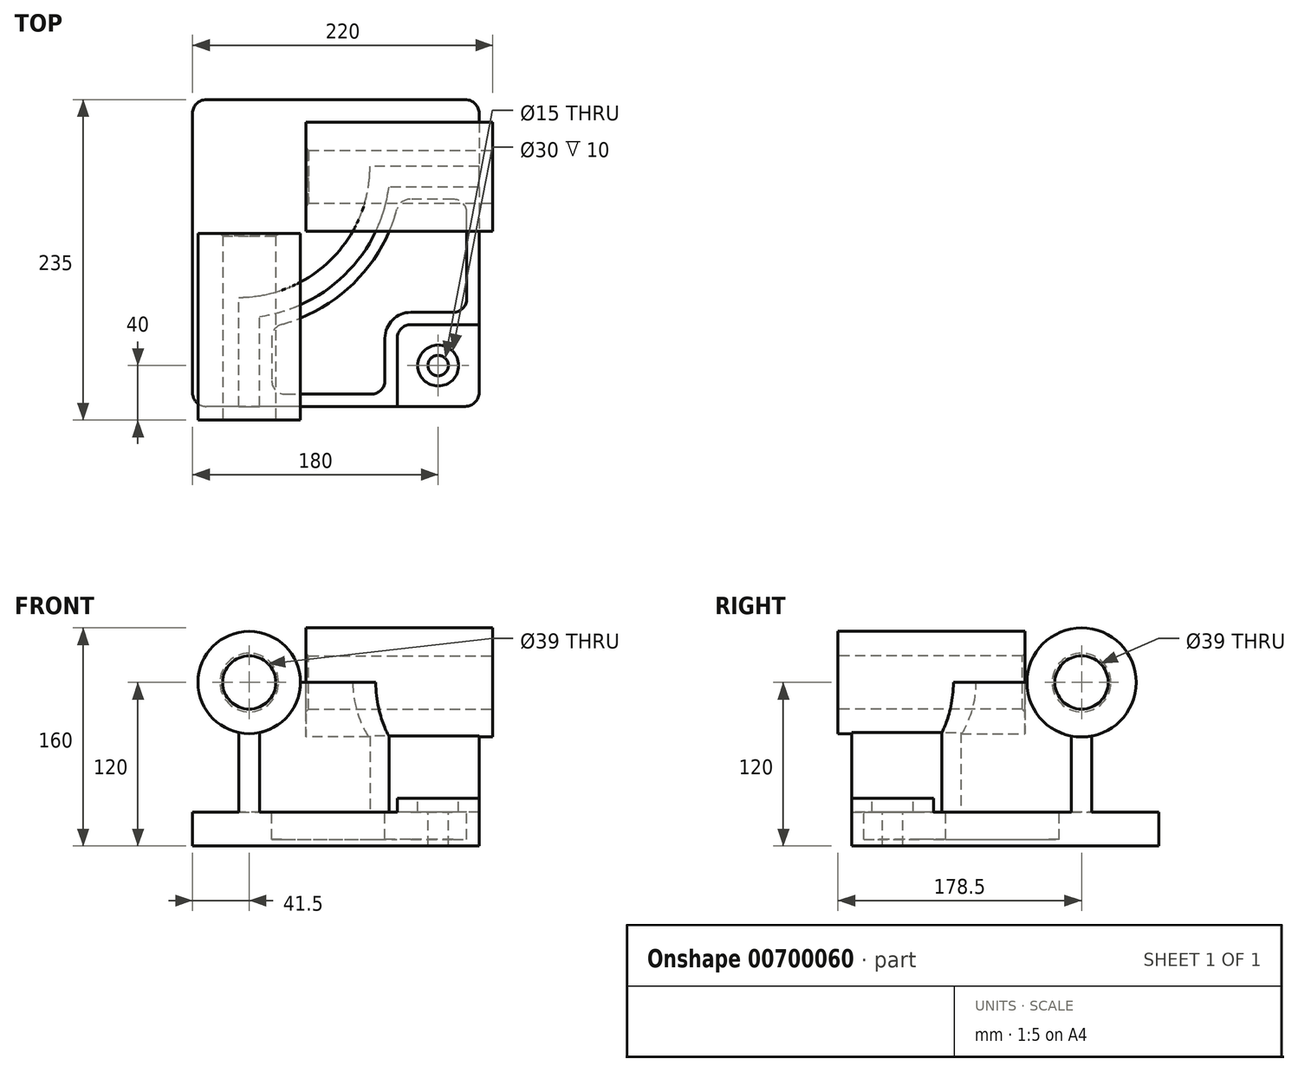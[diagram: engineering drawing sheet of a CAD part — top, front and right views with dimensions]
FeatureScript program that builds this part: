
annotation { "Feature Type Name" : "Feature", "Feature Type Description" : "" }
export const myFeature = defineFeature(function(context is Context, id is Id, definition is map)
    precondition{}
    {
        {
            var Q0;
            Q0=qCreatedBy(makeId("Top.planeOp"),FACE);
            var sketch = newSketch(context, id + "F0", { "sketchPlane" : qUnion([Q0])});
            skLineSegment(sketch, "E0.bottom", {"start": v(105, 112.5) * mm, "end": v(-105, 112.5) * mm});
            skLineSegment(sketch, "E0.top", {"start": v(105, -112.5) * mm, "end": v(-105, -112.5) * mm});
            skLineSegment(sketch, "E0.left", {"start": v(105, 112.5) * mm, "end": v(105, -112.5) * mm});
            skLineSegment(sketch, "E0.right", {"start": v(-105, 112.5) * mm, "end": v(-105, -112.5) * mm});
            skPoint(sketch, "E0.middle", {"position": v(0, 0) * mm});
            skSolve(sketch);
        }
        {
            var Q0;
            Q0=makeQuery(id+"F0.imprint","IMPRINT",FACE,{"disambiguationData":[TD([[makeQuery(id+"F0.imprint","IMPRINT",EDGE,{"derivedFrom":sQuery(id+"F0.wireOp",EDGE,"E0.bottom")}),1.0]])]});
            extrude(context, id + "F1", {"entities" : qUnion([Q0]), "depth" : 25 * mm, "offsetDistance" : 25 * mm});
        }
        {
            var Q0;
            Q0=makeQuery(id+"F1.opExtrude","CAP_FACE",FACE,{"disambiguationData":[OSD([sQuery(id+"F0.wireOp",EDGE,"E0.bottom"),sQuery(id+"F0.wireOp",EDGE,"E0.top"),sQuery(id+"F0.wireOp",EDGE,"E0.left"),sQuery(id+"F0.wireOp",EDGE,"E0.right")])],"isStart":false});
            var sketch = newSketch(context, id + "F2", { "sketchPlane" : qUnion([Q0])});
            skLineSegment(sketch, "E1", {"start": v(-71, -112.5) * mm, "end": v(-71, -32.5) * mm});
            skLineSegment(sketch, "E2", {"start": v(105, 63.5) * mm, "end": v(25, 63.5) * mm});
            skArc(sketch, "E3", {"start": v(-71, -32.5) * mm, "mid": v(-3.12, -4.38) * mm, "end": v(25, 63.5) * mm});
            skLineSegment(sketch, "E4", {"start": v(-71, 63.5) * mm, "end": v(25, 63.5) * mm, "construction": true});
            skLineSegment(sketch, "E5", {"start": v(-71, 63.5) * mm, "end": v(-71, -32.5) * mm, "construction": true});
            skLineSegment(sketch, "E6.0", {"start": v(-56, -112.5) * mm, "end": v(-56, -46.48) * mm});
            skArc(sketch, "E6.1", {"start": v(-56, -46.48) * mm, "mid": v(7.49, -14.99) * mm, "end": v(38.98, 48.5) * mm});
            skLineSegment(sketch, "E6.2", {"start": v(105, 48.5) * mm, "end": v(38.98, 48.5) * mm});
            skLineSegment(sketch, "E7.0", {"start": v(105, 112.5) * mm, "end": v(105, -112.5) * mm});
            skLineSegment(sketch, "E8.0", {"start": v(105, -112.5) * mm, "end": v(-105, -112.5) * mm});
            skSolve(sketch);
        }
        {
            var Q0;
            {var subQ2=sQuery(id+"F2.wireOp",EDGE,"E1");Q0=makeQuery(id+"F2.imprint","IMPRINT",FACE,{"disambiguationData":[TD([[makeQuery(id+"F2.imprint","IMPRINT",EDGE,{"derivedFrom":subQ2}),-1.0]])]});}
            extrude(context, id + "F3", {"entities" : qUnion([Q0]), "operationType" : NewBodyOperationType.ADD, "depth" : 95 * mm, "offsetDistance" : 25 * mm});
        }
        {
            var Q0;
            Q0=makeQuery(id+"F3.boolean.opBoolean","MERGE",FACE,{"derivedFrom":[makeQuery(id+"F1.opExtrude","SWEPT_FACE",FACE,{"disambiguationData":[OSD([sQuery(id+"F0.wireOp",EDGE,"E0.top")])]}),makeQuery(id+"F3.opExtrude","SWEPT_FACE",FACE,{"disambiguationData":[OSD([sQuery(id+"F2.wireOp",EDGE,"E8.0")])]})]});
            var sketch = newSketch(context, id + "F4", { "sketchPlane" : qUnion([Q0])});
            skCircle(sketch, "E9", {"center": v(-63.5, 120) * mm, "radius": 37.5 * mm});
            skSolve(sketch);
        }
        {
            var Q0;
            Q0 = qSketchRegion(id + "F4", true);
            extrude(context, id + "F5", {"entities" : qUnion([Q0]), "operationType" : NewBodyOperationType.ADD, "depth" : 10 * mm, "offsetDistance" : 25 * mm, "hasSecondDirection" : true, "secondDirectionOppositeDirection" : true, "secondDirectionDepth" : (137 - 10) * mm});
        }
        {
            var Q0;
            Q0=makeQuery(id+"F3.boolean.opBoolean","MERGE",FACE,{"derivedFrom":[makeQuery(id+"F1.opExtrude","SWEPT_FACE",FACE,{"disambiguationData":[OSD([sQuery(id+"F0.wireOp",EDGE,"E0.left")])]}),makeQuery(id+"F3.opExtrude","SWEPT_FACE",FACE,{"disambiguationData":[OSD([sQuery(id+"F2.wireOp",EDGE,"E7.0")])]})]});
            var sketch = newSketch(context, id + "F6", { "sketchPlane" : qUnion([Q0])});
            skCircle(sketch, "E10", {"center": v(56, 120) * mm, "radius": 40 * mm});
            skSolve(sketch);
        }
        {
            var Q0;
            Q0 = qSketchRegion(id + "F6", true);
            extrude(context, id + "F7", {"entities" : qUnion([Q0]), "operationType" : NewBodyOperationType.ADD, "depth" : 10 * mm, "offsetDistance" : 25 * mm, "hasSecondDirection" : true, "secondDirectionOppositeDirection" : true, "secondDirectionDepth" : (137 - 10) * mm});
        }
        {
            var Q0;
            {var subQ0=sQuery(id+"F0.wireOp",EDGE,"E0.left");var subQ1=sQuery(id+"F0.wireOp",EDGE,"E0.top");Q0=makeQuery(id+"F3.boolean.opBoolean","SPLIT",FACE,{"disambiguationData":[TD([makeQuery(id+"F3.opExtrude","SWEPT_FACE",FACE,{"disambiguationData":[OSD([sQuery(id+"F2.wireOp",EDGE,"E6.0")])]})])],"derivedFrom":makeQuery(id+"F1.opExtrude","CAP_FACE",FACE,{"disambiguationData":[OSD([sQuery(id+"F0.wireOp",EDGE,"E0.bottom"),subQ1,subQ0,sQuery(id+"F0.wireOp",EDGE,"E0.right")])],"isStart":false})});}
            var sketch = newSketch(context, id + "F8", { "sketchPlane" : qUnion([Q0])});
            skLineSegment(sketch, "E11.bottom", {"start": v(105, -112.5) * mm, "end": v(45, -112.5) * mm});
            skLineSegment(sketch, "E11.top", {"start": v(105, -52.5) * mm, "end": v(45, -52.5) * mm});
            skLineSegment(sketch, "E11.left", {"start": v(105, -112.5) * mm, "end": v(105, -52.5) * mm});
            skLineSegment(sketch, "E11.right", {"start": v(45, -112.5) * mm, "end": v(45, -52.5) * mm});
            skSolve(sketch);
        }
        {
            var Q0;
            Q0 = qSketchRegion(id + "F8", true);
            extrude(context, id + "F9", {"entities" : qUnion([Q0]), "operationType" : NewBodyOperationType.ADD, "depth" : 10 * mm, "offsetDistance" : 25 * mm});
        }
        {
            var Q0;
            Q0=makeQuery(id+"F9.opExtrude","SWEPT_EDGE",EDGE,{"disambiguationData":[OSD([sQuery(id+"F8.wireOp",EDGE,"E11.top"),sQuery(id+"F8.wireOp",EDGE,"E11.right")])]});
            fillet(context, id + "F10", {"entities" : qUnion([Q0]), "radius" : 10 * mm, "tangentPropagation" : true, "allowEdgeOverflow" : false});
        }
        {
            var Q0;
            {var subQ0=sQuery(id+"F0.wireOp",EDGE,"E0.left");var subQ1=sQuery(id+"F0.wireOp",EDGE,"E0.top");Q0=makeQuery(id+"F3.boolean.opBoolean","SPLIT",FACE,{"disambiguationData":[TD([makeQuery(id+"F3.opExtrude","SWEPT_FACE",FACE,{"disambiguationData":[OSD([sQuery(id+"F2.wireOp",EDGE,"E6.0")])]})])],"derivedFrom":makeQuery(id+"F1.opExtrude","CAP_FACE",FACE,{"disambiguationData":[OSD([sQuery(id+"F0.wireOp",EDGE,"E0.bottom"),subQ1,subQ0,sQuery(id+"F0.wireOp",EDGE,"E0.right")])],"isStart":false})});}
            var sketch = newSketch(context, id + "F11", { "sketchPlane" : qUnion([Q0])});
            skLineSegment(sketch, "E12.0", {"start": v(-47, -54.08) * mm, "end": v(-47, -103.5) * mm});
            skArc(sketch, "E12.1", {"start": v(46.58, 39.5) * mm, "mid": v(13.85, -21.35) * mm, "end": v(-47, -54.08) * mm});
            skLineSegment(sketch, "E12.2", {"start": v(-47, -103.5) * mm, "end": v(36, -103.5) * mm});
            skLineSegment(sketch, "E12.3", {"start": v(96, 39.5) * mm, "end": v(46.58, 39.5) * mm});
            skLineSegment(sketch, "E12.4", {"start": v(36, -103.5) * mm, "end": v(36, -62.5) * mm});
            skArc(sketch, "E12.5", {"start": v(36, -62.5) * mm, "mid": v(41.56, -49.06) * mm, "end": v(55, -43.5) * mm});
            skLineSegment(sketch, "E12.6", {"start": v(55, -43.5) * mm, "end": v(96, -43.5) * mm});
            skLineSegment(sketch, "E12.7", {"start": v(96, -43.5) * mm, "end": v(96, 39.5) * mm});
            skSolve(sketch);
        }
        {
            var Q0;
            Q0=makeQuery(id+"F11.imprint","IMPRINT",FACE,{"disambiguationData":[TD([[makeQuery(id+"F11.imprint","IMPRINT",EDGE,{"derivedFrom":sQuery(id+"F11.wireOp",EDGE,"E12.0")}),1.0]])]});
            extrude(context, id + "F12", {"entities" : qUnion([Q0]), "operationType" : NewBodyOperationType.REMOVE, "oppositeDirection" : true, "depth" : (25 - 5) * mm, "offsetDistance" : 25 * mm});
        }
        {
            var Q0;
            Q0=makeQuery(id+"F9.opExtrude","CAP_FACE",FACE,{"disambiguationData":[OSD([sQuery(id+"F8.wireOp",EDGE,"E11.bottom"),sQuery(id+"F8.wireOp",EDGE,"E11.top"),sQuery(id+"F8.wireOp",EDGE,"E11.left"),sQuery(id+"F8.wireOp",EDGE,"E11.right")])],"isStart":false});
            var sketch = newSketch(context, id + "F13", { "sketchPlane" : qUnion([Q0])});
            skCircle(sketch, "E13", {"center": v(75, -82.5) * mm, "radius": 15 * mm});
            skSolve(sketch);
        }
        {
            var Q0;
            Q0=sQuery(id+"F13.wireOp",VERTEX,"E13.center");
            var Q1;
            Q1=makeQuery(id+"F1.opExtrude","SWEPT_BODY",BODY,{"disambiguationData":[OSD([sQuery(id+"F0.wireOp",EDGE,"E0.bottom"),sQuery(id+"F0.wireOp",EDGE,"E0.top"),sQuery(id+"F0.wireOp",EDGE,"E0.left"),sQuery(id+"F0.wireOp",EDGE,"E0.right")])]});
            hole(context, id + "F14", {"style" : HoleStyle.C_BORE, "endStyle" : HoleEndStyle.THROUGH, "holeDiameter" : 15 * mm, "cBoreDiameter" : 30 * mm, "cBoreDepth" : 10 * mm, "majorDiameter" : 5 * mm, "isTappedThrough" : true, "tappedDepth" : 12 * mm, "tapClearance" : 3, "locations" : qUnion([Q0]), "scope" : qUnion([Q1])});
        }
        {
            var Q0;
            Q0=makeQuery(id+"F12.boolean.opBoolean","COPY",EDGE,{"derivedFrom":makeQuery(id+"F12.opExtrude","SWEPT_EDGE",EDGE,{"disambiguationData":[OSD([sQuery(id+"F11.wireOp",EDGE,"E12.0"),sQuery(id+"F11.wireOp",EDGE,"E12.1")])]})});
            var Q1;
            Q1=makeQuery(id+"F12.boolean.opBoolean","COPY",EDGE,{"derivedFrom":makeQuery(id+"F12.opExtrude","SWEPT_EDGE",EDGE,{"disambiguationData":[OSD([sQuery(id+"F11.wireOp",EDGE,"E12.1"),sQuery(id+"F11.wireOp",EDGE,"E12.3")])]})});
            var Q2;
            Q2=makeQuery(id+"F12.boolean.opBoolean","COPY",EDGE,{"derivedFrom":makeQuery(id+"F12.opExtrude","SWEPT_EDGE",EDGE,{"disambiguationData":[OSD([sQuery(id+"F11.wireOp",EDGE,"E12.0"),sQuery(id+"F11.wireOp",EDGE,"E12.2")])]})});
            var Q3;
            Q3=makeQuery(id+"F12.boolean.opBoolean","COPY",EDGE,{"derivedFrom":makeQuery(id+"F12.opExtrude","SWEPT_EDGE",EDGE,{"disambiguationData":[OSD([sQuery(id+"F11.wireOp",EDGE,"E12.3"),sQuery(id+"F11.wireOp",EDGE,"E12.7")])]})});
            var Q4;
            Q4=makeQuery(id+"F12.boolean.opBoolean","COPY",EDGE,{"derivedFrom":makeQuery(id+"F12.opExtrude","SWEPT_EDGE",EDGE,{"disambiguationData":[OSD([sQuery(id+"F11.wireOp",EDGE,"E12.6"),sQuery(id+"F11.wireOp",EDGE,"E12.7")])]})});
            var Q5;
            Q5=makeQuery(id+"F12.boolean.opBoolean","COPY",EDGE,{"derivedFrom":makeQuery(id+"F12.opExtrude","SWEPT_EDGE",EDGE,{"disambiguationData":[OSD([sQuery(id+"F11.wireOp",EDGE,"E12.2"),sQuery(id+"F11.wireOp",EDGE,"E12.4")])]})});
            fillet(context, id + "F15", {"entities" : qUnion([Q0, Q1, Q2, Q3, Q4, Q5]), "radius" : 10 * mm, "tangentPropagation" : true, "allowEdgeOverflow" : false});
        }
        {
            var Q0;
            Q0=makeQuery(id+"F5.opExtrude","CAP_FACE",FACE,{"disambiguationData":[OSD([sQuery(id+"F4.wireOp",EDGE,"E9")])],"isStart":false});
            var sketch = newSketch(context, id + "F16", { "sketchPlane" : qUnion([Q0])});
            skCircle(sketch, "E14", {"center": v(-63.5, 120) * mm, "radius": 19.5 * mm});
            skSolve(sketch);
        }
        {
            var Q0;
            Q0 = qSketchRegion(id + "F16", true);
            extrude(context, id + "F17", {"entities" : qUnion([Q0]), "operationType" : NewBodyOperationType.REMOVE, "endBound" : BoundingType.THROUGH_ALL, "oppositeDirection" : true, "depth" : 25 * mm, "offsetDistance" : 25 * mm});
        }
        {
            var Q0;
            Q0=makeQuery(id+"F7.opExtrude","CAP_FACE",FACE,{"disambiguationData":[OSD([sQuery(id+"F6.wireOp",EDGE,"E10")])],"isStart":false});
            var sketch = newSketch(context, id + "F18", { "sketchPlane" : qUnion([Q0])});
            skCircle(sketch, "E15", {"center": v(56, 120) * mm, "radius": 19.5 * mm});
            skSolve(sketch);
        }
        {
            var Q0;
            Q0 = qSketchRegion(id + "F18", true);
            extrude(context, id + "F19", {"entities" : qUnion([Q0]), "operationType" : NewBodyOperationType.REMOVE, "endBound" : BoundingType.THROUGH_ALL, "oppositeDirection" : true, "depth" : 25 * mm, "offsetDistance" : 25 * mm});
        }
        {
            var Q0;
            Q0=makeQuery(id+"F17.boolean.opBoolean","COPY",EDGE,{"derivedFrom":makeQuery(id+"F17.opExtrude","CAP_EDGE",EDGE,{"disambiguationData":[OSD([sQuery(id+"F16.wireOp",EDGE,"E14")])],"isStart":true})});
            var Q1;
            Q1=makeQuery(id+"F19.boolean.opBoolean","COPY",EDGE,{"derivedFrom":makeQuery(id+"F19.opExtrude","CAP_EDGE",EDGE,{"disambiguationData":[OSD([sQuery(id+"F18.wireOp",EDGE,"E15")])],"isStart":true})});
            var Q2;
            Q2=makeQuery(id+"F19.boolean.opBoolean","INTERSECT",EDGE,{"derivedFrom":[makeQuery(id+"F7.opExtrude","CAP_FACE",FACE,{"disambiguationData":[OSD([sQuery(id+"F6.wireOp",EDGE,"E10")])],"isStart":true}),makeQuery(id+"F19.opExtrude","SWEPT_FACE",FACE,{"disambiguationData":[OSD([sQuery(id+"F18.wireOp",EDGE,"E15")])]})]});
            var Q3;
            Q3=makeQuery(id+"F17.boolean.opBoolean","INTERSECT",EDGE,{"derivedFrom":[makeQuery(id+"F5.opExtrude","CAP_FACE",FACE,{"disambiguationData":[OSD([sQuery(id+"F4.wireOp",EDGE,"E9")])],"isStart":true}),makeQuery(id+"F17.opExtrude","SWEPT_FACE",FACE,{"disambiguationData":[OSD([sQuery(id+"F16.wireOp",EDGE,"E14")])]})]});
            chamfer(context, id + "F20", {"entities" : qUnion([Q0, Q1, Q2, Q3]), "width" : 2 * mm, "tangentPropagation" : true});
        }
        {
            var Q0;
            Q0=makeQuery(id+"F1.opExtrude","SWEPT_EDGE",EDGE,{"disambiguationData":[OSD([sQuery(id+"F0.wireOp",EDGE,"E0.top"),sQuery(id+"F0.wireOp",EDGE,"E0.right")])]});
            var Q1;
            Q1=makeQuery(id+"F9.boolean.opBoolean","MERGE",EDGE,{"derivedFrom":[makeQuery(id+"F1.opExtrude","SWEPT_EDGE",EDGE,{"disambiguationData":[OSD([sQuery(id+"F0.wireOp",EDGE,"E0.top"),sQuery(id+"F0.wireOp",EDGE,"E0.left")])]}),makeQuery(id+"F9.opExtrude","SWEPT_EDGE",EDGE,{"disambiguationData":[OSD([sQuery(id+"F8.wireOp",EDGE,"E11.bottom"),sQuery(id+"F8.wireOp",EDGE,"E11.left")])]})]});
            var Q2;
            Q2=makeQuery(id+"F1.opExtrude","SWEPT_EDGE",EDGE,{"disambiguationData":[OSD([sQuery(id+"F0.wireOp",EDGE,"E0.bottom"),sQuery(id+"F0.wireOp",EDGE,"E0.left")])]});
            var Q3;
            Q3=makeQuery(id+"F1.opExtrude","SWEPT_EDGE",EDGE,{"disambiguationData":[OSD([sQuery(id+"F0.wireOp",EDGE,"E0.bottom"),sQuery(id+"F0.wireOp",EDGE,"E0.right")])]});
            fillet(context, id + "F21", {"entities" : qUnion([Q0, Q1, Q2, Q3]), "radius" : 10 * mm, "tangentPropagation" : true, "allowEdgeOverflow" : false});
        }
    });
